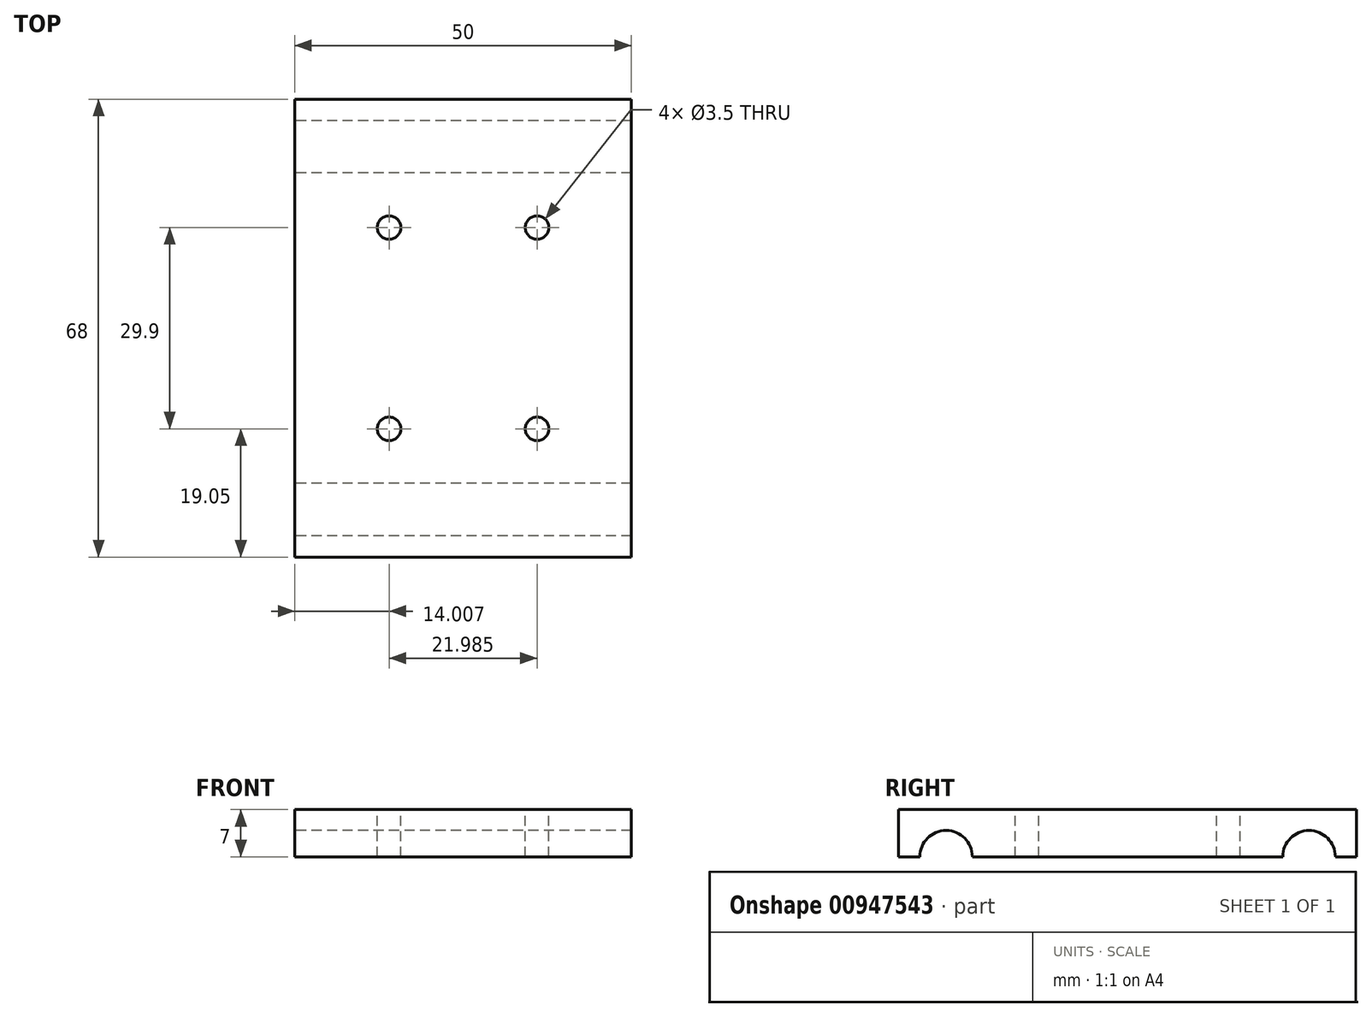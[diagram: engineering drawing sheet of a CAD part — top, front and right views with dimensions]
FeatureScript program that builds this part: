
annotation { "Feature Type Name" : "Feature", "Feature Type Description" : "" }
export const myFeature = defineFeature(function(context is Context, id is Id, definition is map)
    precondition{}
    {
        {
            var Q0;
            Q0=qCreatedBy(makeId("Right.planeOp"),FACE);
            var sketch = newSketch(context, id + "F0", { "sketchPlane" : qUnion([Q0])});
            skLineSegment(sketch, "E0.top", {"start": v(34, 7) * mm, "end": v(-34, 7) * mm});
            skLineSegment(sketch, "E0.left", {"start": v(34, 0) * mm, "end": v(34, 7) * mm});
            skLineSegment(sketch, "E0.right", {"start": v(-34, 0) * mm, "end": v(-34, 7) * mm});
            skPoint(sketch, "E0.middle", {"position": v(0, 0) * mm});
            skLineSegment(sketch, "E1", {"start": v(0, 0) * mm, "end": v(23.05, 0) * mm, "construction": true});
            skArc(sketch, "E2", {"start": v(30.85, 0) * mm, "mid": v(26.95, 3.9) * mm, "end": v(23.05, 0) * mm});
            skLineSegment(sketch, "E3", {"start": v(0, 7) * mm, "end": v(0, -7) * mm, "construction": true});
            skArc(sketch, "E4.MirrorC", {"start": v(-30.85, 0) * mm, "mid": v(-26.95, 3.9) * mm, "end": v(-23.05, 0) * mm});
            skLineSegment(sketch, "E5", {"start": v(-34, 0) * mm, "end": v(-30.85, 0) * mm});
            skPoint(sketch, "E6.orphan", {"position": v(-34, -7) * mm});
            skPoint(sketch, "E7.orphan", {"position": v(34, -7) * mm});
            skLineSegment(sketch, "E8.trimOffspring", {"start": v(-23.05, 0) * mm, "end": v(23.05, 0) * mm});
            skLineSegment(sketch, "E9.trimOffspring", {"start": v(30.85, 0) * mm, "end": v(34, 0) * mm});
            skSolve(sketch);
        }
        {
            var Q0;
            Q0=qSketchRegion(id+"F0",true);
            extrude(context, id + "F1", {"entities" : qUnion([Q0]), "depth" : 50 * mm, "offsetDistance" : 25 * mm});
        }
        {
            var Q0;
            Q0=makeQuery(id+"F1.opExtrude","SWEPT_FACE",FACE,{"disambiguationData":[OSD([sQuery(id+"F0.wireOp",EDGE,"E0.top")])]});
            var sketch = newSketch(context, id + "F2", { "sketchPlane" : qUnion([Q0])});
            skLineSegment(sketch, "E10", {"start": v(0, 34) * mm, "end": v(50, -34) * mm, "construction": true});
            skLineSegment(sketch, "E11", {"start": v(0, -34) * mm, "end": v(50, 34) * mm, "construction": true});
            skLineSegment(sketch, "E12.bottom", {"start": v(40, 14.95) * mm, "end": v(10, 14.95) * mm, "construction": true});
            skLineSegment(sketch, "E12.top", {"start": v(40, -14.95) * mm, "end": v(10, -14.95) * mm, "construction": true});
            skLineSegment(sketch, "E12.left", {"start": v(40, 14.95) * mm, "end": v(40, -14.95) * mm, "construction": true});
            skLineSegment(sketch, "E12.right", {"start": v(10, 14.95) * mm, "end": v(10, -14.95) * mm, "construction": true});
            skPoint(sketch, "E12.middle", {"position": v(25, 0) * mm});
            skPoint(sketch, "E13", {"position": v(14, 14.95) * mm});
            skPoint(sketch, "E14", {"position": v(36, 14.95) * mm});
            skPoint(sketch, "E15", {"position": v(14, -14.95) * mm});
            skPoint(sketch, "E16", {"position": v(36, -14.95) * mm});
            skSolve(sketch);
        }
        {
            var Q0;
            Q0=sQuery(id+"F2.wireOp",VERTEX,"E13");
            var Q1;
            Q1=sQuery(id+"F2.wireOp",VERTEX,"E14");
            var Q2;
            Q2=sQuery(id+"F2.wireOp",VERTEX,"E15");
            var Q3;
            Q3=sQuery(id+"F2.wireOp",VERTEX,"E16");
            var Q4;
            Q4=makeQuery(id+"F1.opExtrude","SWEPT_BODY",BODY,{"disambiguationData":[OSD([sQuery(id+"F0.wireOp",EDGE,"E0.bottom"),sQuery(id+"F0.wireOp",EDGE,"E0.top"),sQuery(id+"F0.wireOp",EDGE,"E0.left"),sQuery(id+"F0.wireOp",EDGE,"E0.right"),sQuery(id+"F0.wireOp",EDGE,"E2"),sQuery(id+"F0.wireOp",EDGE,"E4.MirrorC")])]});
            hole(context, id + "F3", {"style" : HoleStyle.SIMPLE, "endStyle" : HoleEndStyle.THROUGH, "holeDiameter" : 3.5 * mm, "majorDiameter" : 5 * mm, "isTappedThrough" : true, "tappedDepth" : 12 * mm, "tapClearance" : 3, "locations" : qUnion([Q0, Q1, Q2, Q3]), "scope" : qUnion([Q4])});
        }
    });
